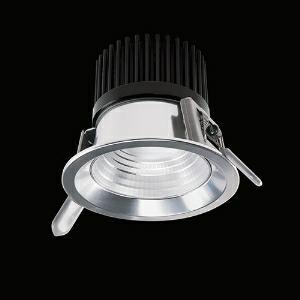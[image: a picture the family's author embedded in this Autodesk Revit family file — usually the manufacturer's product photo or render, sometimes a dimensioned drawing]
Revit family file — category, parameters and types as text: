
# Revit family: spectral_myral_myral_3500-830-m
name_source: partatom
category: Lighting Fixtures
revit_build: Autodesk Revit 2016 (Build: 20150220_1215(x64)
units: mm (PartAtom-declared; Revit-internal decimal feet)

## family parameters
Cut with Voids When Loaded = No
Host = Face
Light Source = No
Part Type = Normal
Room Calculation Point = No
Round Connector Dimension = Use Diameter
Shared = No

## types (1)
- SPECTRAL MYRAL (1 x )
    Apparent Load = 0 VA
    Approval mark = CE
    CIE Flux Codes = 82 99 100 100 100
    Control Gear = Electronic transformer
    Default Elevation = 1800 mm
    Description = SPG0320180
MYRAL recessed spot

Design:
    Height = 0 mm  [stored 0 ft]
    Lamp = 1 x
    Lamp count = 1
    Length = 120 mm
    Luminous efficacy = 0 lm/W
    Manufacturer = Ridi
    ModVariant = No
    Model = MYRAL 3500-830-M
    Mounting Place = Ceiling
    Mounting Type = Recessed
    Number of Poles = 1
    OnlyDefault = Yes
    Power Factor = 1
    Product Name = SPECTRAL MYRAL
    Product group = Downlight recessed
    ProductGroupID = 400
    Protection Class = Protection class
    Protection Degree = IP 20
    RlxData = <blob elided: 38673 chars, md5=f1de87b7>
    Socket = socket
    Standby Power = 0 W
    System Light Flux = 0 lm
    System Power = 0 W
    Type Image = myral_04.jpg
    URL = http://reluxnet.relux.com
    VarID = ---
    Voltage = 0 V
    Weight = 0.00 kg
    Width = 0 mm  [stored 0 ft]

note: [stored X ft] marks values corroborated as IEEE doubles in the binary element streams (Revit-internal decimal feet)

## geometry (parser evidence)
native form markers: Sweep x11
no freeform markers — native parametric forms only
